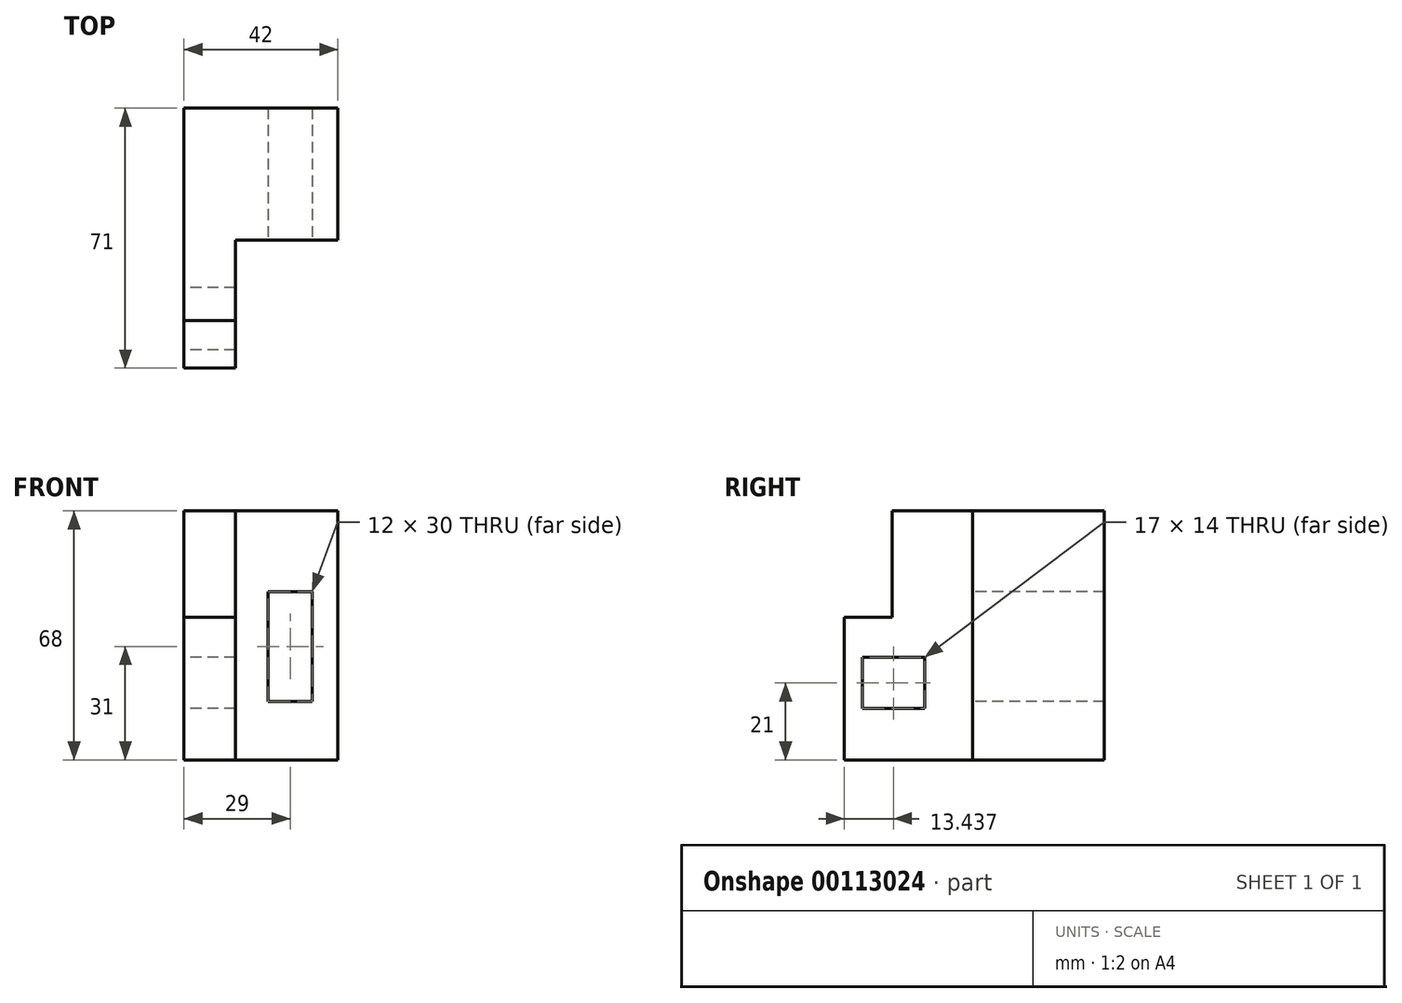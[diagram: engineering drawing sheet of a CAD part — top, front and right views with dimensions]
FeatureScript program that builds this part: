
annotation { "Feature Type Name" : "Feature", "Feature Type Description" : "" }
export const myFeature = defineFeature(function(context is Context, id is Id, definition is map)
    precondition{}
    {
        {
            var Q0;
            Q0=qCreatedBy(makeId("Front.planeOp"),FACE);
            var sketch = newSketch(context, id + "F0", { "sketchPlane" : qUnion([Q0])});
            skLineSegment(sketch, "E0.bottom", {"start": v(21, -34) * mm, "end": v(-21, -34) * mm});
            skLineSegment(sketch, "E0.top", {"start": v(21, 34) * mm, "end": v(-21, 34) * mm});
            skLineSegment(sketch, "E0.left", {"start": v(21, -34) * mm, "end": v(21, 34) * mm});
            skLineSegment(sketch, "E0.right", {"start": v(-21, -34) * mm, "end": v(-21, 34) * mm});
            skPoint(sketch, "E0.middle", {"position": v(0, 0) * mm});
            skLineSegment(sketch, "E1", {"start": v(-7, 34) * mm, "end": v(-7, 5) * mm});
            skLineSegment(sketch, "E2", {"start": v(-7, 5) * mm, "end": v(-21, 5) * mm});
            skLineSegment(sketch, "E3", {"start": v(-7, 5) * mm, "end": v(-7, -34) * mm});
            skLineSegment(sketch, "E4", {"start": v(-7, -34) * mm, "end": v(-21, -34) * mm});
            skSolve(sketch);
        }
        {
            var Q0;
            Q0 = qSketchRegion(id + "F0", true);
            extrude(context, id + "F1", {"entities" : qUnion([Q0]), "depth" : 36 * mm});
        }
        {
            var Q0;
            Q0=makeQuery(id+"F1.opExtrude","CAP_FACE",FACE,{"disambiguationData":[OSD([sQuery(id+"F0.wireOp",EDGE,"E0.bottom"),sQuery(id+"F0.wireOp",EDGE,"E0.top"),sQuery(id+"F0.wireOp",EDGE,"E0.left"),sQuery(id+"F0.wireOp",EDGE,"E0.right"),sQuery(id+"F0.wireOp",EDGE,"E4")])],"isStart":false});
            var sketch = newSketch(context, id + "F2", { "sketchPlane" : qUnion([Q0])});
            skLineSegment(sketch, "E5", {"start": v(-7, 34) * mm, "end": v(-7, 5) * mm});
            skLineSegment(sketch, "E6", {"start": v(-7, 5) * mm, "end": v(-21, 5) * mm});
            skSolve(sketch);
        }
        {
            var Q0;
            Q0 = qSketchRegion(id + "F2", true);
            var Q1;
            {var subQ0=sQuery(id+"F2.wireOp",EDGE,"E5");Q1=makeQuery(id+"F2.imprint","IMPRINT",FACE,{"disambiguationData":[TD([[makeQuery(id+"F2.imprint","IMPRINT",EDGE,{"derivedFrom":subQ0}),-1.0]])]});}
            extrude(context, id + "F3", {"entities" : qUnion([Q0, Q1]), "operationType" : NewBodyOperationType.ADD, "depth" : 22 * mm});
        }
        {
            var Q0;
            Q0=makeQuery(id+"F1.opExtrude","CAP_FACE",FACE,{"disambiguationData":[OSD([sQuery(id+"F0.wireOp",EDGE,"E0.bottom"),sQuery(id+"F0.wireOp",EDGE,"E0.top"),sQuery(id+"F0.wireOp",EDGE,"E0.left"),sQuery(id+"F0.wireOp",EDGE,"E0.right"),sQuery(id+"F0.wireOp",EDGE,"E4")])],"isStart":false});
            var sketch = newSketch(context, id + "F4", { "sketchPlane" : qUnion([Q0])});
            skLineSegment(sketch, "E7", {"start": v(-7, 5) * mm, "end": v(-7, -34) * mm});
            skLineSegment(sketch, "E8", {"start": v(-7, -34) * mm, "end": v(-21, -34) * mm});
            skSolve(sketch);
        }
        {
            var Q0;
            Q0=makeQuery(id+"F4.imprint","IMPRINT",FACE,{"disambiguationData":[TD([[makeQuery(id+"F4.imprint","IMPRINT",EDGE,{"derivedFrom":sQuery(id+"F4.wireOp",EDGE,"E7")}),-1.0]])]});
            extrude(context, id + "F5", {"entities" : qUnion([Q0]), "operationType" : NewBodyOperationType.ADD, "depth" : 35 * mm});
        }
        {
            var Q0;
            {var subQ0=sQuery(id+"F0.wireOp",EDGE,"E0.right");Q0=makeQuery(id+"F5.boolean.opBoolean","MERGE",FACE,{"derivedFrom":[makeQuery(id+"F3.boolean.opBoolean","MERGE",FACE,{"derivedFrom":[makeQuery(id+"F1.opExtrude","SWEPT_FACE",FACE,{"disambiguationData":[OSD([subQ0])]}),makeQuery(id+"F3.opExtrude","SWEPT_FACE",FACE,{"disambiguationData":[OSD([subQ0])]})]}),makeQuery(id+"F5.opExtrude","SWEPT_FACE",FACE,{"disambiguationData":[OSD([subQ0])]})]});}
            var sketch = newSketch(context, id + "F6", { "sketchPlane" : qUnion([Q0])});
            skLineSegment(sketch, "E9", {"start": v(58, 5) * mm, "end": v(36.27, 5) * mm});
            skLineSegment(sketch, "E10", {"start": v(36.27, 5) * mm, "end": v(36.27, -34) * mm});
            skLineSegment(sketch, "E11", {"start": v(36.27, -34) * mm, "end": v(71, -34) * mm});
            skLineSegment(sketch, "E12", {"start": v(71, -34) * mm, "end": v(71, 5) * mm});
            skLineSegment(sketch, "E13", {"start": v(71, 5) * mm, "end": v(58, 5) * mm});
            skLineSegment(sketch, "E14.bottom", {"start": v(49.06, -6) * mm, "end": v(66.06, -6) * mm});
            skLineSegment(sketch, "E14.top", {"start": v(49.06, -20) * mm, "end": v(66.06, -20) * mm});
            skLineSegment(sketch, "E14.left", {"start": v(49.06, -6) * mm, "end": v(49.06, -20) * mm});
            skLineSegment(sketch, "E14.right", {"start": v(66.06, -6) * mm, "end": v(66.06, -20) * mm});
            skPoint(sketch, "E14.middle", {"position": v(57.56, -13) * mm});
            skSolve(sketch);
        }
        {
            var Q0;
            Q0=makeQuery(id+"F6.imprint","IMPRINT",FACE,{"disambiguationData":[TD([[makeQuery(id+"F6.imprint","IMPRINT",EDGE,{"derivedFrom":sQuery(id+"F6.wireOp",EDGE,"E14.bottom")}),-1.0]])]});
            extrude(context, id + "F7", {"entities" : qUnion([Q0]), "operationType" : NewBodyOperationType.REMOVE, "oppositeDirection" : true, "depth" : 25 * mm});
        }
        {
            var Q0;
            Q0=makeQuery(id+"F1.opExtrude","CAP_FACE",FACE,{"disambiguationData":[OSD([sQuery(id+"F0.wireOp",EDGE,"E0.bottom"),sQuery(id+"F0.wireOp",EDGE,"E0.top"),sQuery(id+"F0.wireOp",EDGE,"E0.left"),sQuery(id+"F0.wireOp",EDGE,"E0.right"),sQuery(id+"F0.wireOp",EDGE,"E4")])],"isStart":false});
            var sketch = newSketch(context, id + "F8", { "sketchPlane" : qUnion([Q0])});
            skLineSegment(sketch, "E15.bottom", {"start": v(14, -18) * mm, "end": v(2, -18) * mm});
            skLineSegment(sketch, "E15.top", {"start": v(14, 12) * mm, "end": v(2, 12) * mm});
            skLineSegment(sketch, "E15.left", {"start": v(14, -18) * mm, "end": v(14, 12) * mm});
            skLineSegment(sketch, "E15.right", {"start": v(2, -18) * mm, "end": v(2, 12) * mm});
            skPoint(sketch, "E15.middle", {"position": v(8, -3) * mm});
            skSolve(sketch);
        }
        {
            var Q0;
            Q0=makeQuery(id+"F8.imprint","IMPRINT",FACE,{"disambiguationData":[TD([[makeQuery(id+"F8.imprint","IMPRINT",EDGE,{"derivedFrom":sQuery(id+"F8.wireOp",EDGE,"E15.bottom")}),-1.0]])]});
            extrude(context, id + "F9", {"entities" : qUnion([Q0]), "operationType" : NewBodyOperationType.REMOVE, "oppositeDirection" : true, "depth" : 40 * mm});
        }
    });
